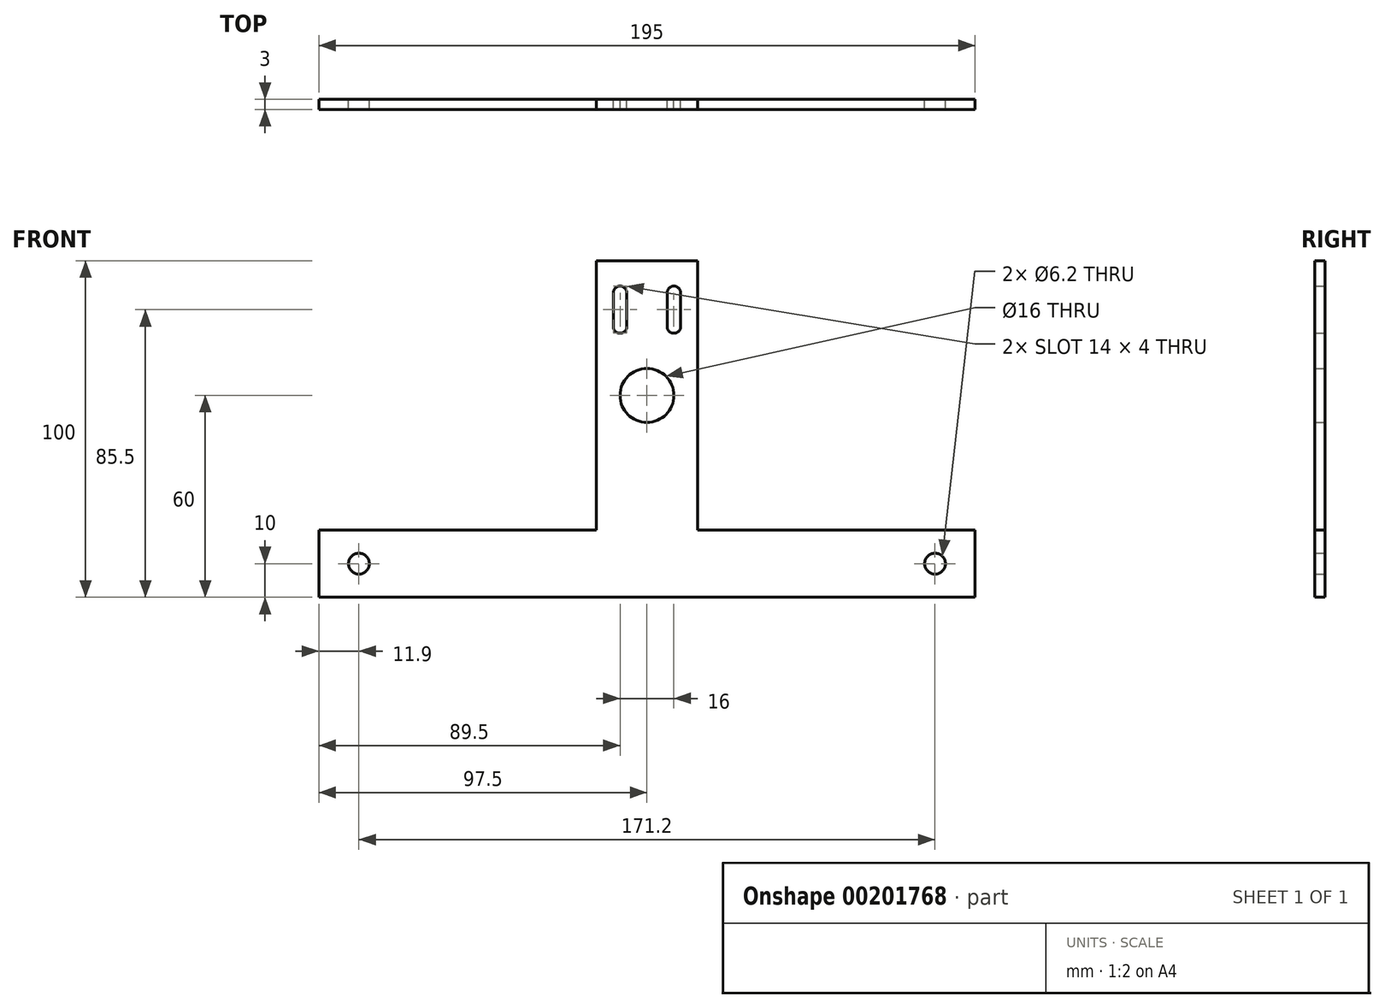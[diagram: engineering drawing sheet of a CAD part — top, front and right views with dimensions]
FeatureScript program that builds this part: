
annotation { "Feature Type Name" : "Feature", "Feature Type Description" : "" }
export const myFeature = defineFeature(function(context is Context, id is Id, definition is map)
    precondition{}
    {
        {
            var Q0;
            Q0=qCreatedBy(makeId("Front.planeOp"),FACE);
            var sketch = newSketch(context, id + "F0", { "sketchPlane" : qUnion([Q0])});
            skLineSegment(sketch, "E0", {"start": v(0, 0) * mm, "end": v(-97.5, 0) * mm});
            skLineSegment(sketch, "E1", {"start": v(-97.5, 0) * mm, "end": v(-97.5, 20) * mm});
            skLineSegment(sketch, "E2", {"start": v(-97.5, 20) * mm, "end": v(-15, 20) * mm});
            skLineSegment(sketch, "E3", {"start": v(-15, 20) * mm, "end": v(-15, 100) * mm});
            skLineSegment(sketch, "E4", {"start": v(-15, 100) * mm, "end": v(0, 100) * mm});
            skLineSegment(sketch, "E5.MirrorCS", {"start": v(97.5, 0) * mm, "end": v(97.5, 20) * mm});
            skLineSegment(sketch, "E6.MirrorCS", {"start": v(0, 0) * mm, "end": v(97.5, 0) * mm});
            skLineSegment(sketch, "E7.MirrorCS", {"start": v(15, 20) * mm, "end": v(15, 100) * mm});
            skLineSegment(sketch, "E8.MirrorCS", {"start": v(97.5, 20) * mm, "end": v(15, 20) * mm});
            skLineSegment(sketch, "E9.MirrorCS", {"start": v(15, 100) * mm, "end": v(0, 100) * mm});
            skCircle(sketch, "E10", {"center": v(-85.6, 10) * mm, "radius": 3.1 * mm});
            skPoint(sketch, "E10.centerSnap0", {"position": v(-97.5, 10) * mm});
            skCircle(sketch, "E11", {"center": v(85.6, 10) * mm, "radius": 3.1 * mm});
            skPoint(sketch, "E11.centerSnap0", {"position": v(97.5, 10) * mm});
            skCircle(sketch, "E12", {"center": v(0, 60) * mm, "radius": 8 * mm});
            skLineSegment(sketch, "E13", {"start": v(-10, 90.5) * mm, "end": v(-10, 80.5) * mm});
            skLineSegment(sketch, "E14", {"start": v(-6, 90.5) * mm, "end": v(-6, 80.5) * mm});
            skArc(sketch, "E15", {"start": v(-10, 90.5) * mm, "mid": v(-8, 92.5) * mm, "end": v(-6, 90.5) * mm});
            skArc(sketch, "E16", {"start": v(-6, 80.5) * mm, "mid": v(-8, 78.5) * mm, "end": v(-10, 80.5) * mm});
            skArc(sketch, "E17.MirrorCS", {"start": v(6, 80.5) * mm, "mid": v(8, 78.5) * mm, "end": v(10, 80.5) * mm});
            skArc(sketch, "E18.MirrorCS", {"start": v(10, 90.5) * mm, "mid": v(8, 92.5) * mm, "end": v(6, 90.5) * mm});
            skLineSegment(sketch, "E19.MirrorCS", {"start": v(6, 90.5) * mm, "end": v(6, 80.5) * mm});
            skLineSegment(sketch, "E20.MirrorCS", {"start": v(10, 90.5) * mm, "end": v(10, 80.5) * mm});
            skSolve(sketch);
        }
        {
            var Q0;
            Q0=qSketchRegion(id+"F0",true);
            extrude(context, id + "F1", {"entities" : qUnion([Q0]), "depth" : 3 * mm});
        }
    });
